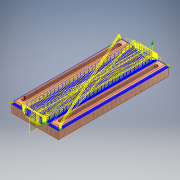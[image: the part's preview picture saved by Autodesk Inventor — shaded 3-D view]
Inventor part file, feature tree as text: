
AUTODESK INVENTOR PART (.ipt)
format: ipt  version: 2018 (Build 220112000, 112)  size: 833,536 bytes
history: native  units: mm
features: extrude x3, sketch x3, chamfer x1, plane x1, mirror x1, fillet x1
ambient origin geometry x8: Origin, YZ Plane, XZ Plane, XY Plane, X Axis, Y Axis, Z Axis, Center Point
bodies: Solid1 (feature_tree)
feature tree (10):
  extrude  "Extrusion1"  Depth=200.0mm
  extrude  "Extrusion2"  Depth=7.5mm
  chamfer  "Chamfer1"  Distance=7.5mm
  extrude  "Extrusion5"  Depth=10.0mm TaperAngle=0.0deg
  plane  "Work Plane1"
  mirror  "Mirror1"
  fillet  "Fillet3"  Radius=3.0mm
  sketch  "Sketch2"  dims[d0=85.0mm d1=200.0mm]
  sketch  "Sketch3"  dims[d2=19.0mm d3=0.0mm d5=7.5mm]
  sketch  "Sketch11"  dims[d6=7.5mm d7=7.5mm d8=10.0mm d9=0.0mm d21=3.0mm d22=2.0mm d23=45.0deg d24=5.0mm d25=0.0mm d29=3.0mm d30=6.749036mm]
